# Revit family: Sanitary_Sanitary-Accessories_AXOR_42849CHN-AXOR-Universal-Circular-Shaving
name_source: partatom
category: Furniture
revit_build: Autodesk Revit 2018 (Build: 20170223_1515(x64)
units: mm (PartAtom-declared; Revit-internal decimal feet)

## family parameters
Always vertical = No
Cut with Voids When Loaded = No
OmniClass Number = 23.40.20.00
OmniClass Title = General Furniture and Specialties
Room Calculation Point = No
Shared = No
Work Plane-Based = Yes

## types (3) — shared parameters
Always visible = Yes
BIMobject category = Sanitary Accessories
Default Elevation = 1219.2 mm  [stored 4 ft]
Design country = Germany
Edition number = 1
IFC Classification = Sanitary Terminal
Installation instructions = https://www.axor-design.com
Manufacturer country = Germany
Manufacturer name = AXOR
Material 2 = AXOR - Universal Circular - Mirror
Material main = Metal
Material secondary = Chrome
Product Guid = 56f744ce-7fe3-4abb-be7d-b5bdc542ed5b
Product SKU = 42849CHN
Product data url = https://www.bimobject.com
Product family = AXOR Universal Circular
Product group = Mirrors
Product name = 42849CHN AXOR Universal Circular Shaving mirror
Product url = https://www.axor-design.com
QR code = https://www.bimobject.com
Technical description = https://www.axor-design.com

## per-type parameters (varying)
| type | Material 1 |
| 677 Matte Black | AXOR - Universal Circular - 677 Matte Black |
| 707 Matt White | AXOR - Universal Circular - 707 Matt White |
| 007 Chrome | AXOR - Universal Circular - 007 Chrome |

note: [stored X ft] marks values corroborated as IEEE doubles in the binary element streams (Revit-internal decimal feet)

## geometry (parser evidence)
native form markers: Sweep x2
no freeform markers — native parametric forms only
